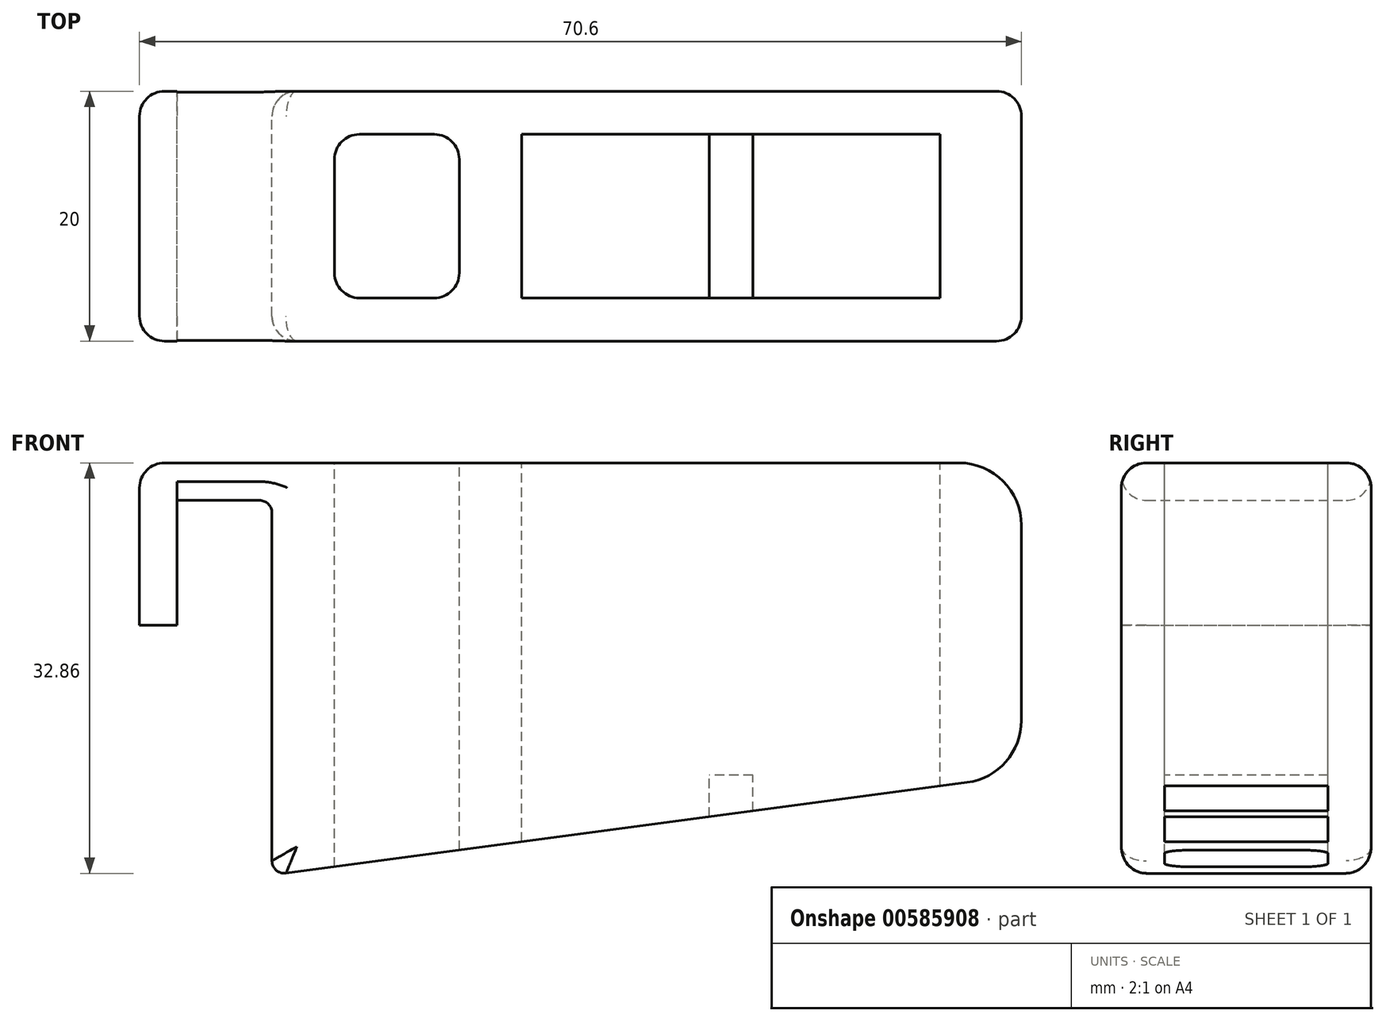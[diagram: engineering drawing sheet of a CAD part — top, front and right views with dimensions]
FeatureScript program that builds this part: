
annotation { "Feature Type Name" : "Feature", "Feature Type Description" : "" }
export const myFeature = defineFeature(function(context is Context, id is Id, definition is map)
    precondition{}
    {
        {
            var Q0;
            Q0=qCreatedBy(makeId("Front.planeOp"),FACE);
            var sketch = newSketch(context, id + "F0", { "sketchPlane" : qUnion([Q0])});
            skLineSegment(sketch, "E0", {"start": v(0, 0) * mm, "end": v(3, 0) * mm});
            skLineSegment(sketch, "E1", {"start": v(3, 0) * mm, "end": v(3, 10) * mm});
            skLineSegment(sketch, "E2", {"start": v(3, 10) * mm, "end": v(10.6, 10) * mm});
            skLineSegment(sketch, "E3", {"start": v(10.6, 10) * mm, "end": v(10.6, -20) * mm});
            skLineSegment(sketch, "E4", {"start": v(70.6, -12) * mm, "end": v(70.6, 13) * mm});
            skLineSegment(sketch, "E5", {"start": v(0, 0) * mm, "end": v(0, 13) * mm});
            skLineSegment(sketch, "E6", {"start": v(0, 13) * mm, "end": v(13.6, 13) * mm});
            skLineSegment(sketch, "E7", {"start": v(13.6, 13) * mm, "end": v(70.6, 13) * mm});
            skLineSegment(sketch, "E8", {"start": v(10.6, -20) * mm, "end": v(70.6, -12) * mm});
            skSolve(sketch);
        }
        {
            var Q0;
            Q0 = qSketchRegion(id + "F0", true);
            extrude(context, id + "F1", {"entities" : qUnion([Q0]), "depth" : 20 * mm, "offsetDistance" : 25 * mm});
        }
        {
            var Q0;
            Q0=makeQuery(id+"F1.opExtrude","SWEPT_EDGE",EDGE,{"disambiguationData":[OSD([sQuery(id+"F0.wireOp",EDGE,"E4"),sQuery(id+"F0.wireOp",EDGE,"HfLkwnr6-hDRT-BLom-Skms-wcUbn8wcjBA7")])]});
            fillet(context, id + "F2", {"entities" : qUnion([Q0]), "radius" : 5 * mm, "tangentPropagation" : true, "allowEdgeOverflow" : false});
        }
        {
            var Q0;
            Q0=makeQuery(id+"F1.opExtrude","SWEPT_EDGE",EDGE,{"disambiguationData":[OSD([sQuery(id+"F0.wireOp",EDGE,"E5"),sQuery(id+"F0.wireOp",EDGE,"E6")])]});
            fillet(context, id + "F3", {"entities" : qUnion([Q0]), "radius" : 2 * mm, "tangentPropagation" : true, "allowEdgeOverflow" : false});
        }
        {
            var Q0;
            Q0=makeQuery(id+"F1.opExtrude","SWEPT_EDGE",EDGE,{"disambiguationData":[OSD([sQuery(id+"F0.wireOp",EDGE,"E3"),sQuery(id+"F0.wireOp",EDGE,"xQi4YeKC-KPdL-J0U9-7hjr-gP99MdsDSgcv")])]});
            fillet(context, id + "F4", {"entities" : qUnion([Q0]), "radius" : 1 * mm, "tangentPropagation" : true, "allowEdgeOverflow" : false});
        }
        {
            var Q0;
            Q0=makeQuery(id+"F1.opExtrude","SWEPT_FACE",FACE,{"disambiguationData":[OSD([sQuery(id+"F0.wireOp",EDGE,"E6"),sQuery(id+"F0.wireOp",EDGE,"E7")])]});
            var sketch = newSketch(context, id + "F5", { "sketchPlane" : qUnion([Q0])});
            skLineSegment(sketch, "E9", {"start": v(0, 0) * mm, "end": v(0, -10) * mm});
            skLineSegment(sketch, "E10", {"start": v(0, -10) * mm, "end": v(30.6, -10) * mm});
            skLineSegment(sketch, "E11", {"start": v(30.6, -10) * mm, "end": v(30.6, -3.45) * mm});
            skLineSegment(sketch, "E12", {"start": v(30.6, -3.45) * mm, "end": v(30.6, -16.55) * mm});
            skLineSegment(sketch, "E13", {"start": v(30.6, -16.55) * mm, "end": v(64.1, -16.55) * mm});
            skLineSegment(sketch, "E14", {"start": v(64.1, -16.55) * mm, "end": v(64.1, -3.45) * mm});
            skLineSegment(sketch, "E15", {"start": v(64.1, -3.45) * mm, "end": v(30.6, -3.45) * mm});
            skSolve(sketch);
        }
        {
            var Q0;
            {var subQ0=sQuery(id+"F5.wireOp",EDGE,"E13");Q0=makeQuery(id+"F5.imprint","IMPRINT",FACE,{"disambiguationData":[TD([[makeQuery(id+"F5.imprint","IMPRINT",EDGE,{"derivedFrom":subQ0}),1.0]])]});}
            extrude(context, id + "F6", {"entities" : qUnion([Q0]), "operationType" : NewBodyOperationType.REMOVE, "oppositeDirection" : true, "depth" : 25 * mm, "offsetDistance" : 25 * mm});
        }
        {
            var Q0;
            Q0=makeQuery(id+"F6.boolean.opBoolean","COPY",FACE,{"derivedFrom":makeQuery(id+"F6.opExtrude","CAP_FACE",FACE,{"disambiguationData":[OSD([sQuery(id+"F5.wireOp",EDGE,"E12"),sQuery(id+"F5.wireOp",EDGE,"E13"),sQuery(id+"F5.wireOp",EDGE,"E14"),sQuery(id+"F5.wireOp",EDGE,"E15")])],"isStart":false})});
            var sketch = newSketch(context, id + "F7", { "sketchPlane" : qUnion([Q0])});
            skLineSegment(sketch, "E16.bottom", {"start": v(30.6, -3.45) * mm, "end": v(45.6, -3.45) * mm});
            skLineSegment(sketch, "E16.top", {"start": v(30.6, -16.55) * mm, "end": v(45.6, -16.55) * mm});
            skLineSegment(sketch, "E16.left", {"start": v(30.6, -3.45) * mm, "end": v(30.6, -16.55) * mm});
            skLineSegment(sketch, "E16.right", {"start": v(45.6, -3.45) * mm, "end": v(45.6, -16.55) * mm});
            skLineSegment(sketch, "E17.bottom", {"start": v(64.1, -3.45) * mm, "end": v(49.1, -3.45) * mm});
            skLineSegment(sketch, "E17.top", {"start": v(64.1, -16.55) * mm, "end": v(49.1, -16.55) * mm});
            skLineSegment(sketch, "E17.left", {"start": v(64.1, -3.45) * mm, "end": v(64.1, -16.55) * mm});
            skLineSegment(sketch, "E17.right", {"start": v(49.1, -3.45) * mm, "end": v(49.1, -16.55) * mm});
            skSolve(sketch);
        }
        {
            var Q0;
            Q0 = qSketchRegion(id + "F7", true);
            extrude(context, id + "F8", {"entities" : qUnion([Q0]), "operationType" : NewBodyOperationType.REMOVE, "oppositeDirection" : true, "depth" : 25 * mm, "offsetDistance" : 25 * mm});
        }
        {
            var Q0;
            Q0=makeQuery(id+"F1.opExtrude","SWEPT_FACE",FACE,{"disambiguationData":[OSD([sQuery(id+"F0.wireOp",EDGE,"E6"),sQuery(id+"F0.wireOp",EDGE,"E7")])]});
            var sketch = newSketch(context, id + "F9", { "sketchPlane" : qUnion([Q0])});
            skLineSegment(sketch, "E18", {"start": v(30.6, -3.45) * mm, "end": v(25.6, -3.45) * mm});
            skLineSegment(sketch, "E19", {"start": v(25.6, -3.45) * mm, "end": v(25.6, -16.55) * mm});
            skLineSegment(sketch, "E20", {"start": v(25.6, -16.55) * mm, "end": v(15.6, -16.55) * mm});
            skLineSegment(sketch, "E21", {"start": v(15.6, -16.55) * mm, "end": v(15.6, -3.45) * mm});
            skLineSegment(sketch, "E22", {"start": v(15.6, -3.45) * mm, "end": v(25.6, -3.45) * mm});
            skSolve(sketch);
        }
        {
            var Q0;
            Q0=makeQuery(id+"F9.imprint","IMPRINT",FACE,{"disambiguationData":[TD([[makeQuery(id+"F9.imprint","IMPRINT",EDGE,{"derivedFrom":sQuery(id+"F9.wireOp",EDGE,"E19")}),-1.0]])]});
            extrude(context, id + "F10", {"entities" : qUnion([Q0]), "operationType" : NewBodyOperationType.REMOVE, "oppositeDirection" : true, "depth" : 50 * mm, "offsetDistance" : 25 * mm});
        }
        {
            var Q0;
            Q0=makeQuery(id+"F10.boolean.opBoolean","COPY",EDGE,{"derivedFrom":makeQuery(id+"F10.opExtrude","SWEPT_EDGE",EDGE,{"disambiguationData":[OSD([sQuery(id+"F9.wireOp",EDGE,"E21"),sQuery(id+"F9.wireOp",EDGE,"E22")])]})});
            var Q1;
            Q1=makeQuery(id+"F10.boolean.opBoolean","COPY",EDGE,{"derivedFrom":makeQuery(id+"F10.opExtrude","SWEPT_EDGE",EDGE,{"disambiguationData":[OSD([sQuery(id+"F9.wireOp",EDGE,"E19"),sQuery(id+"F9.wireOp",EDGE,"E22")])]})});
            var Q2;
            Q2=makeQuery(id+"F10.boolean.opBoolean","COPY",EDGE,{"derivedFrom":makeQuery(id+"F10.opExtrude","SWEPT_EDGE",EDGE,{"disambiguationData":[OSD([sQuery(id+"F9.wireOp",EDGE,"E20"),sQuery(id+"F9.wireOp",EDGE,"E21")])]})});
            var Q3;
            Q3=makeQuery(id+"F10.boolean.opBoolean","COPY",EDGE,{"derivedFrom":makeQuery(id+"F10.opExtrude","SWEPT_EDGE",EDGE,{"disambiguationData":[OSD([sQuery(id+"F9.wireOp",EDGE,"E19"),sQuery(id+"F9.wireOp",EDGE,"E20")])]})});
            var Q4;
            Q4=makeQuery(id+"F1.opExtrude","CAP_EDGE",EDGE,{"disambiguationData":[OSD([sQuery(id+"F0.wireOp",EDGE,"E6"),sQuery(id+"F0.wireOp",EDGE,"E7")])],"isStart":false});
            var Q5;
            Q5=makeQuery(id+"F1.opExtrude","CAP_EDGE",EDGE,{"disambiguationData":[OSD([sQuery(id+"F0.wireOp",EDGE,"E6"),sQuery(id+"F0.wireOp",EDGE,"E7")])],"isStart":true});
            fillet(context, id + "F11", {"entities" : qUnion([Q0, Q1, Q2, Q3, Q4, Q5]), "radius" : 2 * mm, "tangentPropagation" : true, "allowEdgeOverflow" : false});
        }
    });
